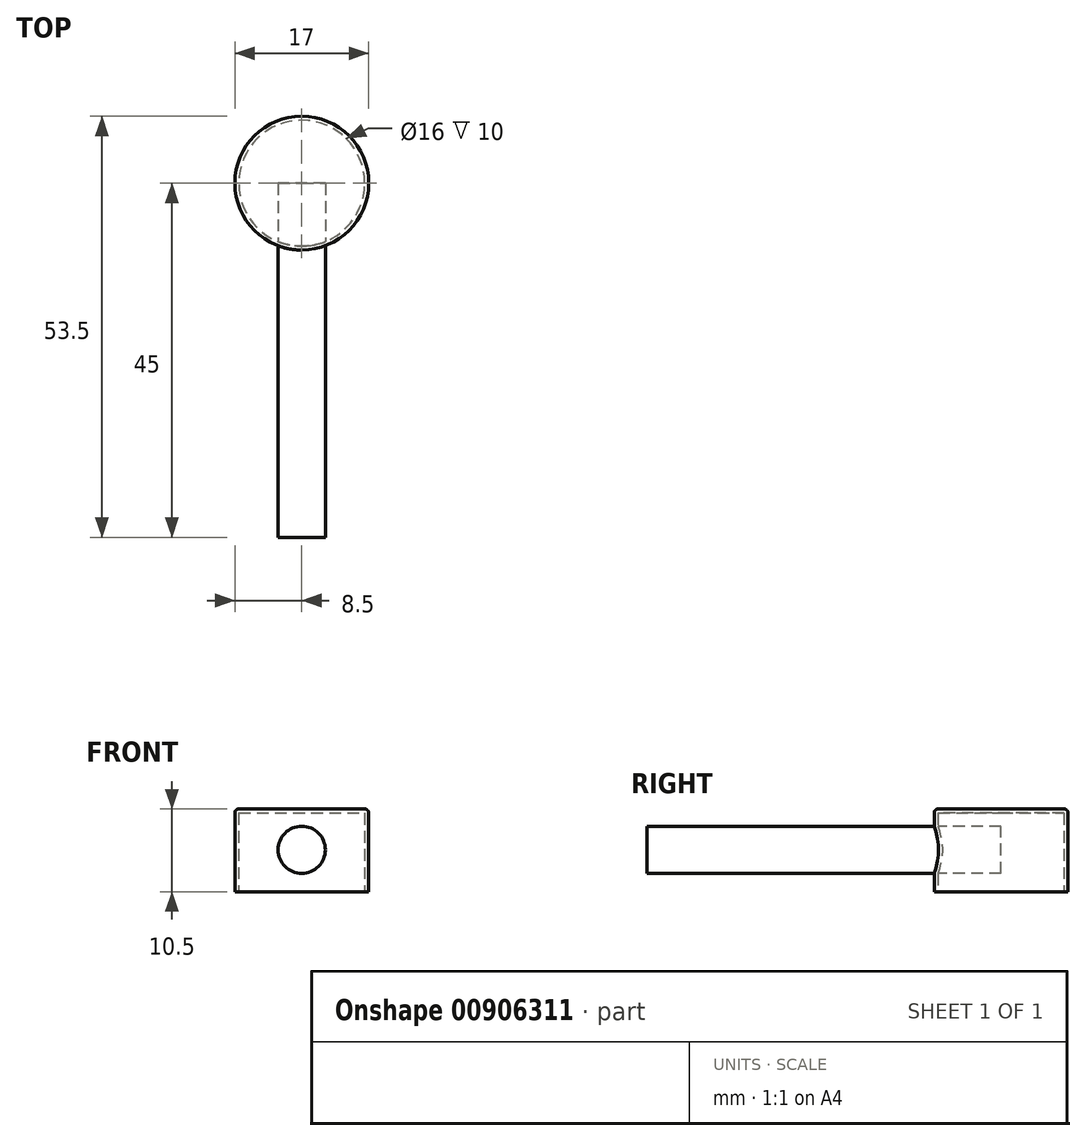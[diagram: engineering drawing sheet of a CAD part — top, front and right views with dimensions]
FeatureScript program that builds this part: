
annotation { "Feature Type Name" : "Feature", "Feature Type Description" : "" }
export const myFeature = defineFeature(function(context is Context, id is Id, definition is map)
    precondition{}
    {
        {
            var Q0;
            Q0=qCreatedBy(makeId("Top.planeOp"),FACE);
            var sketch = newSketch(context, id + "F0", { "sketchPlane" : qUnion([Q0])});
            skCircle(sketch, "E0", {"center": v(0, 0) * mm, "radius": 8.5 * mm});
            skCircle(sketch, "E1", {"center": v(0, 0) * mm, "radius": 8 * mm});
            skSolve(sketch);
        }
        {
            var Q0;
            Q0=qCreatedBy(makeId("Front.planeOp"),FACE);
            var sketch = newSketch(context, id + "F1", { "sketchPlane" : qUnion([Q0])});
            skLineSegment(sketch, "E2", {"start": v(8, 0) * mm, "end": v(8, 10) * mm});
            skLineSegment(sketch, "E3", {"start": v(8, 10) * mm, "end": v(0, 10) * mm});
            skLineSegment(sketch, "E4", {"start": v(8.5, 0) * mm, "end": v(8.5, 10) * mm});
            skLineSegment(sketch, "E5", {"start": v(8, 10.5) * mm, "end": v(0, 10.5) * mm});
            skLineSegment(sketch, "E6", {"start": v(0, 10.5) * mm, "end": v(0, 10) * mm});
            skLineSegment(sketch, "E7", {"start": v(8, 0) * mm, "end": v(8.5, 0) * mm});
            skPoint(sketch, "E8.visualSharp", {"position": v(8.5, 10.5) * mm});
            skArc(sketch, "E8.filletArc", {"start": v(8.5, 10) * mm, "mid": v(8.35, 10.35) * mm, "end": v(8, 10.5) * mm});
            skSolve(sketch);
        }
        {
            var Q0;
            Q0=makeQuery(id+"F1.imprint","IMPRINT",FACE,{"disambiguationData":[TD([[makeQuery(id+"F1.imprint","IMPRINT",EDGE,{"derivedFrom":sQuery(id+"F1.wireOp",EDGE,"E2")}),-1.0]])]});
            var Q1;
            Q1=sQuery(id+"F0.wireOp",EDGE,"E1");
            revolve(context, id + "F2", {"surfaceOperationType" : NewSurfaceOperationType.NEW, "entities" : qUnion([Q0]), "axis" : qUnion([Q1]), "revolveType" : RevolveType.FULL});
        }
        {
            var Q0;
            Q0=qCreatedBy(makeId("Right.planeOp"),FACE);
            var sketch = newSketch(context, id + "F3", { "sketchPlane" : qUnion([Q0])});
            skLineSegment(sketch, "E9", {"start": v(-53, 5.27) * mm, "end": v(-8, 5.27) * mm});
            skSolve(sketch);
        }
        {
            var Q0;
            Q0=qCreatedBy(makeId("Front.planeOp"),FACE);
            var sketch = newSketch(context, id + "F4", { "sketchPlane" : qUnion([Q0])});
            skCircle(sketch, "E10", {"center": v(0, 5.3) * mm, "radius": 3 * mm});
            skSolve(sketch);
        }
        {
            var Q0;
            Q0=makeQuery(id+"F4.imprint","IMPRINT",FACE,{"disambiguationData":[TD([[makeQuery(id+"F4.imprint","IMPRINT",EDGE,{"derivedFrom":sQuery(id+"F4.wireOp",EDGE,"E10")}),1.0]])]});
            var Q1;
            Q1=sQuery(id+"F3.wireOp",EDGE,"E9");
            sweep(context, id + "F5", {"operationType" : NewBodyOperationType.ADD, "profiles" : qUnion([Q0]), "path" : qUnion([Q1])});
        }
    });
